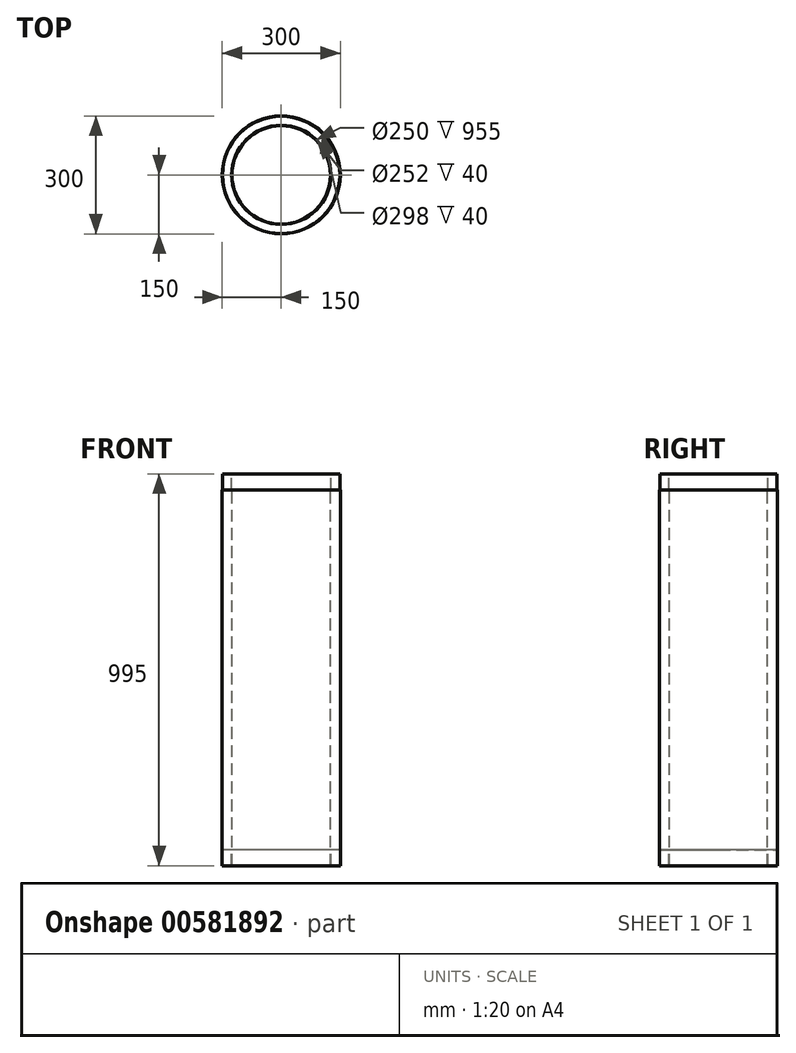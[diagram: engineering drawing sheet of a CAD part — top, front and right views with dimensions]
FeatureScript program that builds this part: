
annotation { "Feature Type Name" : "Feature", "Feature Type Description" : "" }
export const myFeature = defineFeature(function(context is Context, id is Id, definition is map)
    precondition{}
    {
        {
            var Q0;
            Q0=qCreatedBy(makeId("Front.planeOp"),FACE);
            var sketch = newSketch(context, id + "F0", { "sketchPlane" : qUnion([Q0])});
            skLineSegment(sketch, "E0", {"start": v(0, 345.75) * mm, "end": v(0, -558.03) * mm, "construction": true});
            skLineSegment(sketch, "E1", {"start": v(-125, -518.84) * mm, "end": v(-125, 436.16) * mm});
            skLineSegment(sketch, "E2", {"start": v(-125, 436.16) * mm, "end": v(-126, 436.16) * mm});
            skLineSegment(sketch, "E3", {"start": v(-126, 436.16) * mm, "end": v(-126, 476.16) * mm});
            skLineSegment(sketch, "E4", {"start": v(-126, 476.16) * mm, "end": v(-149, 476.16) * mm});
            skLineSegment(sketch, "E5", {"start": v(-149, 476.16) * mm, "end": v(-149, 436.16) * mm});
            skLineSegment(sketch, "E6", {"start": v(-149, 436.16) * mm, "end": v(-150, 436.16) * mm});
            skLineSegment(sketch, "E7", {"start": v(-150, 436.16) * mm, "end": v(-150, -518.84) * mm});
            skLineSegment(sketch, "E8", {"start": v(-150, -518.84) * mm, "end": v(-149, -518.84) * mm});
            skLineSegment(sketch, "E9", {"start": v(-149, -518.84) * mm, "end": v(-149, -478.84) * mm});
            skLineSegment(sketch, "E10", {"start": v(-149, -478.84) * mm, "end": v(-126, -478.84) * mm});
            skLineSegment(sketch, "E11", {"start": v(-126, -478.84) * mm, "end": v(-126, -518.84) * mm});
            skLineSegment(sketch, "E12", {"start": v(-126, -518.84) * mm, "end": v(-125, -518.84) * mm});
            skSolve(sketch);
        }
        {
            var Q0;
            Q0=qSketchRegion(id+"F0",true);
            var Q1;
            Q1=sQuery(id+"F0.wireOp",EDGE,"E0");
            revolve(context, id + "F1", {"entities" : qUnion([Q0]), "axis" : qUnion([Q1]), "revolveType" : RevolveType.FULL});
        }
    });
